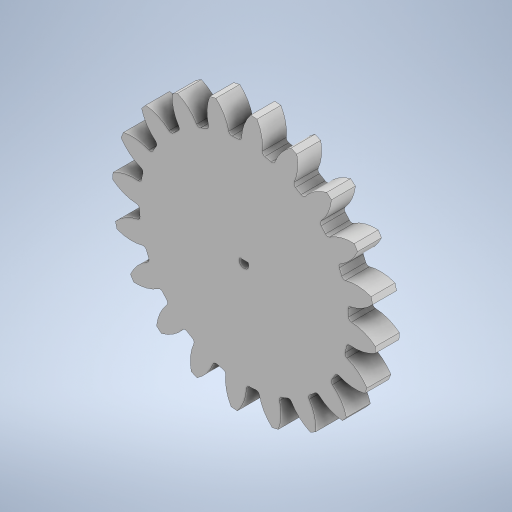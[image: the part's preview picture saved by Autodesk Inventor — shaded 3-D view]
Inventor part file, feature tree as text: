
AUTODESK INVENTOR PART (.ipt)
format: ipt  version: 2023.2 (Build 272271030, 271C)  size: 449,536 bytes
history: native  units: mm
features: extrude x1, fillet x1, pattern_circular x1, sketch x1
ambient origin geometry x8: Origin, YZ Plane, XZ Plane, XY Plane, X Axis, Y Axis, Z Axis, Center Point
bodies: Solid1 (feature_tree)
feature tree (4):
  extrude  "Extrusion1"  Depth=20.0mm TaperAngle=0.0deg
  fillet  "Fillet1"  Radius=2.61mm
  pattern_circular  "Circular Pattern1"  Count=20 Angle=360.0deg
  sketch  "Sketch1"  dims[d8=200.0mm d10=360.0deg d12=20.0mm d13=0.0mm d15=2.61mm d16=200.0mm d17=360.0deg d19=8.05mm d20=2.0mm]
